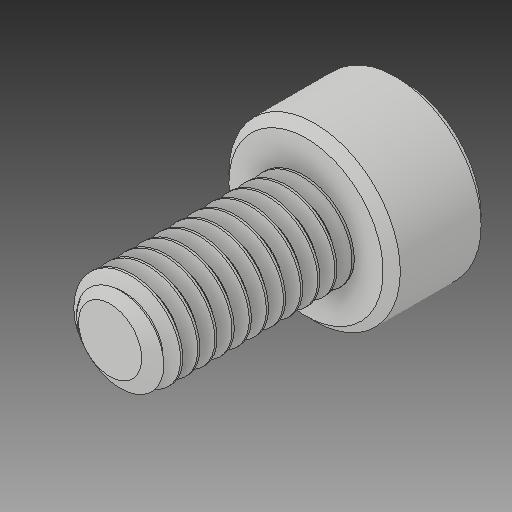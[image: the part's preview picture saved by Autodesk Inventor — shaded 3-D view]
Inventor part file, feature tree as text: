
AUTODESK INVENTOR PART (.ipt)
format: ipt  version: 2019.4 (Build 234330000, 330)  size: 501,248 bytes
history: native  units: in
note: dims shown in document units (in); Inventor stores cm internally (conversion verified against a paired STEP export)
features: chamfer x1
ambient origin geometry x8: Origin, YZ Plane, XZ Plane, XY Plane, X Axis, Y Axis, Z Axis, Center Point
bodies: Solid1 (feature_tree)
feature tree (1):
  chamfer  "Chamfer1"  [1 undecoded]
note: 1 required parameter value undecoded (feature->parameter linkage not recoverable at this tier; creation-order binding heuristic only, values carry confidence <= 0.55)
